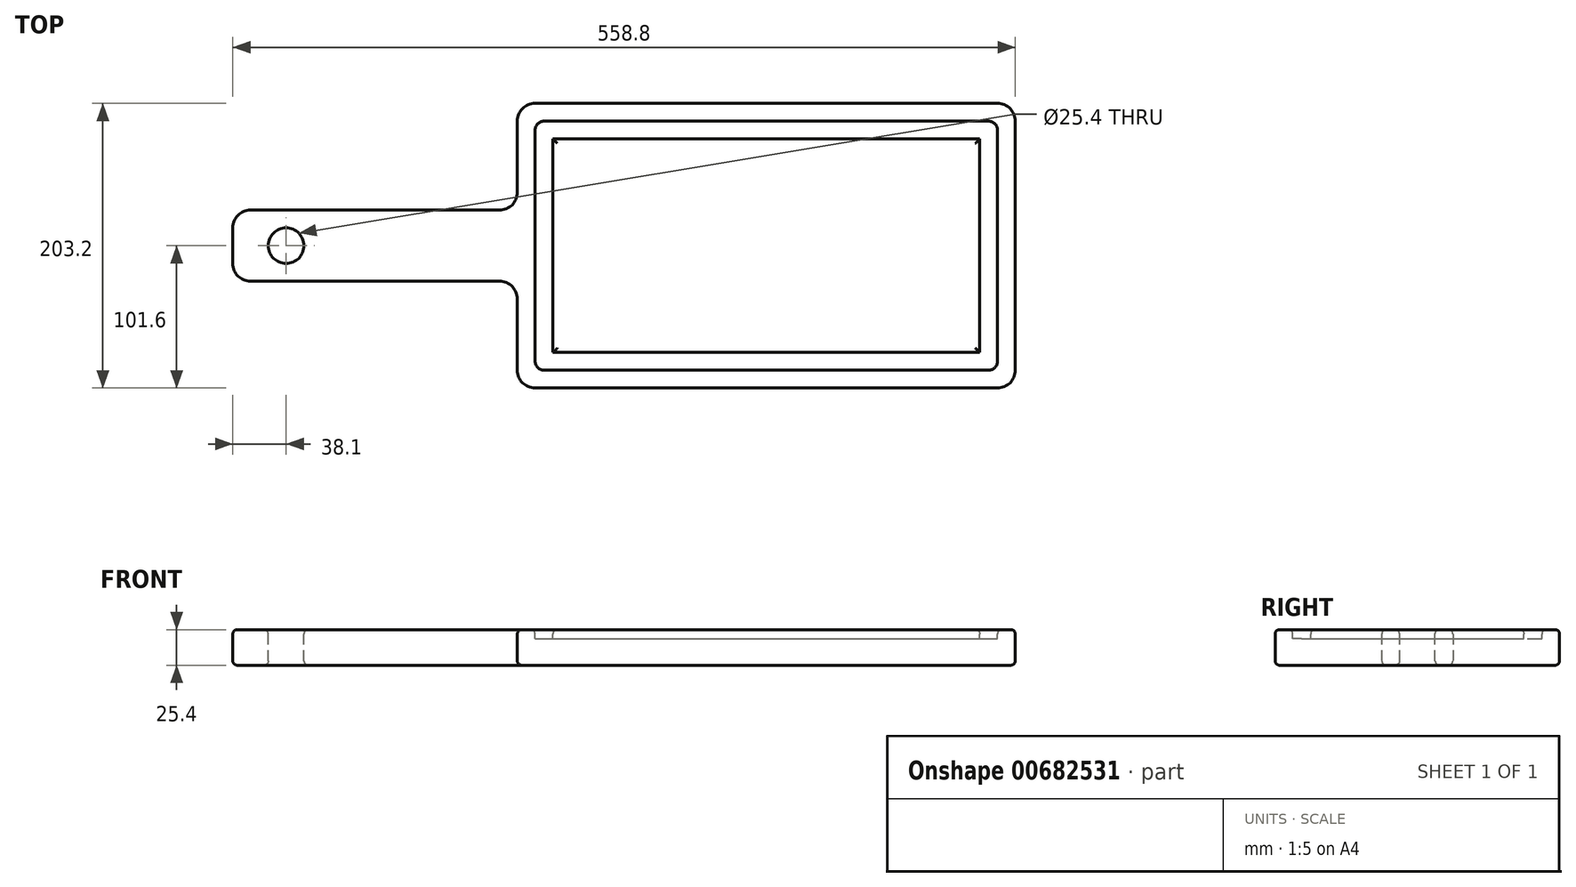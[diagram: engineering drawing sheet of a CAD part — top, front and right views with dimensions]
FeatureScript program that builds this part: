
annotation { "Feature Type Name" : "Feature", "Feature Type Description" : "" }
export const myFeature = defineFeature(function(context is Context, id is Id, definition is map)
    precondition{}
    {
        {
            var Q0;
            Q0=qCreatedBy(makeId("Top.planeOp"),FACE);
            var sketch = newSketch(context, id + "F0", { "sketchPlane" : qUnion([Q0])});
            skLineSegment(sketch, "E0.bottom", {"start": v(0, 0) * mm, "end": v(355.6, 0) * mm});
            skLineSegment(sketch, "E0.top", {"start": v(0, 203.2) * mm, "end": v(355.6, 203.2) * mm});
            skLineSegment(sketch, "E0.left", {"start": v(0, 0) * mm, "end": v(0, 203.2) * mm});
            skLineSegment(sketch, "E0.right", {"start": v(355.6, 0) * mm, "end": v(355.6, 203.2) * mm});
            skLineSegment(sketch, "E1.bottom", {"start": v(0, 127) * mm, "end": v(-203.2, 127) * mm});
            skLineSegment(sketch, "E1.top", {"start": v(0, 76.2) * mm, "end": v(-203.2, 76.2) * mm});
            skLineSegment(sketch, "E1.left", {"start": v(0, 127) * mm, "end": v(0, 76.2) * mm});
            skLineSegment(sketch, "E1.right", {"start": v(-203.2, 127) * mm, "end": v(-203.2, 76.2) * mm});
            skSolve(sketch);
        }
        {
            var Q0;
            {var subQ3=sQuery(id+"F0.wireOp",EDGE,"E0.bottom");Q0=makeQuery(id+"F0.imprint","IMPRINT",FACE,{"disambiguationData":[TD([[makeQuery(id+"F0.imprint","IMPRINT",EDGE,{"derivedFrom":subQ3}),1.0]])]});}
            var Q1;
            Q1=makeQuery(id+"F0.imprint","IMPRINT",FACE,{"disambiguationData":[TD([[makeQuery(id+"F0.imprint","IMPRINT",EDGE,{"derivedFrom":sQuery(id+"F0.wireOp",EDGE,"E1.bottom")}),1.0]])]});
            extrude(context, id + "F1", {"entities" : qUnion([Q0, Q1]), "depth" : 25.4 * mm, "offsetDistance" : 25.4 * mm});
        }
        {
            var Q0;
            Q0=makeQuery(id+"F1.opExtrude","CAP_FACE",FACE,{"disambiguationData":[OSD([sQuery(id+"F0.wireOp",EDGE,"E0.bottom"),sQuery(id+"F0.wireOp",EDGE,"E0.top"),sQuery(id+"F0.wireOp",EDGE,"E0.left"),sQuery(id+"F0.wireOp",EDGE,"E0.right"),sQuery(id+"F0.wireOp",EDGE,"E1.bottom"),sQuery(id+"F0.wireOp",EDGE,"E1.top"),sQuery(id+"F0.wireOp",EDGE,"E1.right")])],"isStart":false});
            var sketch = newSketch(context, id + "F2", { "sketchPlane" : qUnion([Q0])});
            skCircle(sketch, "E2", {"center": v(-165.1, 101.6) * mm, "radius": 12.7 * mm});
            skSolve(sketch);
        }
        {
            var Q0;
            Q0 = qSketchRegion(id + "F2", true);
            extrude(context, id + "F3", {"entities" : qUnion([Q0]), "operationType" : NewBodyOperationType.REMOVE, "oppositeDirection" : true, "depth" : 25.4 * mm, "offsetDistance" : 25.4 * mm});
        }
        {
            var Q0;
            Q0=makeQuery(id+"F1.opExtrude","CAP_FACE",FACE,{"disambiguationData":[OSD([sQuery(id+"F0.wireOp",EDGE,"E0.bottom"),sQuery(id+"F0.wireOp",EDGE,"E0.top"),sQuery(id+"F0.wireOp",EDGE,"E0.left"),sQuery(id+"F0.wireOp",EDGE,"E0.right"),sQuery(id+"F0.wireOp",EDGE,"E1.bottom"),sQuery(id+"F0.wireOp",EDGE,"E1.top"),sQuery(id+"F0.wireOp",EDGE,"E1.right")])],"isStart":false});
            var sketch = newSketch(context, id + "F4", { "sketchPlane" : qUnion([Q0])});
            skLineSegment(sketch, "E3.0", {"start": v(12.7, 12.7) * mm, "end": v(12.7, 76.2) * mm});
            skLineSegment(sketch, "E3.1", {"start": v(12.7, 127) * mm, "end": v(12.7, 190.5) * mm});
            skLineSegment(sketch, "E3.2", {"start": v(12.7, 190.5) * mm, "end": v(342.9, 190.5) * mm});
            skLineSegment(sketch, "E3.3", {"start": v(342.9, 12.7) * mm, "end": v(342.9, 190.5) * mm});
            skLineSegment(sketch, "E3.4", {"start": v(12.7, 12.7) * mm, "end": v(342.9, 12.7) * mm});
            skLineSegment(sketch, "E4", {"start": v(12.7, 127) * mm, "end": v(12.7, 72.3) * mm});
            skLineSegment(sketch, "E5.0", {"start": v(25.4, 25.4) * mm, "end": v(25.4, 76.2) * mm});
            skLineSegment(sketch, "E5.1", {"start": v(25.4, 127) * mm, "end": v(25.4, 177.8) * mm});
            skLineSegment(sketch, "E5.2", {"start": v(25.4, 177.8) * mm, "end": v(330.2, 177.8) * mm});
            skLineSegment(sketch, "E5.3", {"start": v(330.2, 25.4) * mm, "end": v(330.2, 177.8) * mm});
            skLineSegment(sketch, "E5.4", {"start": v(25.4, 25.4) * mm, "end": v(330.2, 25.4) * mm});
            skLineSegment(sketch, "E6", {"start": v(25.4, 127) * mm, "end": v(25.4, 76.2) * mm});
            skSolve(sketch);
        }
        {
            var Q0;
            {var subQ1=sQuery(id+"F4.wireOp",EDGE,"E3.0");Q0=makeQuery(id+"F4.imprint","IMPRINT",FACE,{"disambiguationData":[TD([[makeQuery(id+"F4.imprint","IMPRINT",EDGE,{"derivedFrom":subQ1}),-1.0]])]});}
            extrude(context, id + "F5", {"entities" : qUnion([Q0]), "operationType" : NewBodyOperationType.REMOVE, "oppositeDirection" : true, "depth" : 6.35 * mm, "offsetDistance" : 25.4 * mm});
        }
        {
            var Q0;
            Q0=makeQuery(id+"F5.boolean.opBoolean","COPY",EDGE,{"derivedFrom":makeQuery(id+"F5.opExtrude","SWEPT_EDGE",EDGE,{"disambiguationData":[OSD([sQuery(id+"F4.wireOp",EDGE,"E3.1"),sQuery(id+"F4.wireOp",EDGE,"E3.2")])]})});
            var Q1;
            Q1=makeQuery(id+"F5.boolean.opBoolean","COPY",EDGE,{"derivedFrom":makeQuery(id+"F5.opExtrude","SWEPT_EDGE",EDGE,{"disambiguationData":[OSD([sQuery(id+"F4.wireOp",EDGE,"E3.2"),sQuery(id+"F4.wireOp",EDGE,"E3.3")])]})});
            var Q2;
            Q2=makeQuery(id+"F5.boolean.opBoolean","COPY",EDGE,{"derivedFrom":makeQuery(id+"F5.opExtrude","SWEPT_EDGE",EDGE,{"disambiguationData":[OSD([sQuery(id+"F4.wireOp",EDGE,"E3.3"),sQuery(id+"F4.wireOp",EDGE,"E3.4")])]})});
            var Q3;
            Q3=makeQuery(id+"F5.boolean.opBoolean","COPY",EDGE,{"derivedFrom":makeQuery(id+"F5.opExtrude","SWEPT_EDGE",EDGE,{"disambiguationData":[OSD([sQuery(id+"F4.wireOp",EDGE,"E3.0"),sQuery(id+"F4.wireOp",EDGE,"E3.4")])]})});
            fillet(context, id + "F6", {"entities" : qUnion([Q0, Q1, Q2, Q3]), "radius" : 6.35 * mm, "tangentPropagation" : true, "allowEdgeOverflow" : false});
        }
        {
            var Q0;
            Q0=makeQuery(id+"F1.opExtrude","SWEPT_EDGE",EDGE,{"disambiguationData":[OSD([sQuery(id+"F0.wireOp",EDGE,"E0.bottom"),sQuery(id+"F0.wireOp",EDGE,"E0.left")])]});
            var Q1;
            Q1=makeQuery(id+"F1.opExtrude","SWEPT_EDGE",EDGE,{"disambiguationData":[OSD([sQuery(id+"F0.wireOp",EDGE,"E1.top"),sQuery(id+"F0.wireOp",EDGE,"E1.right")])]});
            var Q2;
            Q2=makeQuery(id+"F1.opExtrude","SWEPT_EDGE",EDGE,{"disambiguationData":[OSD([sQuery(id+"F0.wireOp",EDGE,"E1.bottom"),sQuery(id+"F0.wireOp",EDGE,"E1.right")])]});
            var Q3;
            Q3=makeQuery(id+"F1.opExtrude","SWEPT_EDGE",EDGE,{"disambiguationData":[OSD([sQuery(id+"F0.wireOp",EDGE,"E0.left"),sQuery(id+"F0.wireOp",EDGE,"E1.bottom"),sQuery(id+"F0.wireOp",EDGE,"E1.left")])]});
            var Q4;
            Q4=makeQuery(id+"F1.opExtrude","SWEPT_EDGE",EDGE,{"disambiguationData":[OSD([sQuery(id+"F0.wireOp",EDGE,"E0.top"),sQuery(id+"F0.wireOp",EDGE,"E0.left")])]});
            var Q5;
            Q5=makeQuery(id+"F1.opExtrude","SWEPT_EDGE",EDGE,{"disambiguationData":[OSD([sQuery(id+"F0.wireOp",EDGE,"E0.top"),sQuery(id+"F0.wireOp",EDGE,"E0.right")])]});
            var Q6;
            Q6=makeQuery(id+"F1.opExtrude","SWEPT_EDGE",EDGE,{"disambiguationData":[OSD([sQuery(id+"F0.wireOp",EDGE,"E0.bottom"),sQuery(id+"F0.wireOp",EDGE,"E0.right")])]});
            var Q7;
            Q7=makeQuery(id+"F1.opExtrude","SWEPT_EDGE",EDGE,{"disambiguationData":[OSD([sQuery(id+"F0.wireOp",EDGE,"E0.left"),sQuery(id+"F0.wireOp",EDGE,"E1.top"),sQuery(id+"F0.wireOp",EDGE,"E1.left")])]});
            fillet(context, id + "F7", {"entities" : qUnion([Q0, Q1, Q2, Q3, Q4, Q5, Q6, Q7]), "radius" : 12.7 * mm, "tangentPropagation" : true, "allowEdgeOverflow" : false});
        }
        {
            var Q0;
            Q0=makeQuery(id+"F5.boolean.opBoolean","SPLIT",FACE,{"disambiguationData":[TD([makeQuery(id+"F5.opExtrude","SWEPT_FACE",FACE,{"disambiguationData":[OSD([sQuery(id+"F4.wireOp",EDGE,"E5.2")])]})])],"derivedFrom":makeQuery(id+"F1.opExtrude","CAP_FACE",FACE,{"disambiguationData":[OSD([sQuery(id+"F0.wireOp",EDGE,"E0.bottom"),sQuery(id+"F0.wireOp",EDGE,"E0.top"),sQuery(id+"F0.wireOp",EDGE,"E0.left"),sQuery(id+"F0.wireOp",EDGE,"E0.right"),sQuery(id+"F0.wireOp",EDGE,"E1.bottom"),sQuery(id+"F0.wireOp",EDGE,"E1.top"),sQuery(id+"F0.wireOp",EDGE,"E1.right")])],"isStart":false})});
            var Q1;
            {var subQ0=sQuery(id+"F0.wireOp",EDGE,"E1.right");var subQ1=sQuery(id+"F0.wireOp",EDGE,"E1.top");var subQ2=sQuery(id+"F0.wireOp",EDGE,"E1.bottom");var subQ3=sQuery(id+"F0.wireOp",EDGE,"E0.right");var subQ4=sQuery(id+"F0.wireOp",EDGE,"E0.bottom");var subQ5=sQuery(id+"F0.wireOp",EDGE,"E0.left");var subQ6=sQuery(id+"F0.wireOp",EDGE,"E0.top");Q1=makeQuery(id+"F5.boolean.opBoolean","SPLIT",FACE,{"disambiguationData":[TD([makeQuery(id+"F1.opExtrude","SWEPT_FACE",FACE,{"disambiguationData":[OSD([subQ4])]})])],"derivedFrom":makeQuery(id+"F1.opExtrude","CAP_FACE",FACE,{"disambiguationData":[OSD([subQ4,subQ6,subQ5,subQ3,subQ2,subQ1,subQ0])],"isStart":false})});}
            var Q2;
            Q2=makeQuery(id+"F1.opExtrude","CAP_FACE",FACE,{"disambiguationData":[OSD([sQuery(id+"F0.wireOp",EDGE,"E0.bottom"),sQuery(id+"F0.wireOp",EDGE,"E0.top"),sQuery(id+"F0.wireOp",EDGE,"E0.left"),sQuery(id+"F0.wireOp",EDGE,"E0.right"),sQuery(id+"F0.wireOp",EDGE,"E1.bottom"),sQuery(id+"F0.wireOp",EDGE,"E1.top"),sQuery(id+"F0.wireOp",EDGE,"E1.right")])],"isStart":true});
            fillet(context, id + "F8", {"entities" : qUnion([Q0, Q1, Q2]), "radius" : 3.17 * mm, "tangentPropagation" : true, "allowEdgeOverflow" : false});
        }
    });
